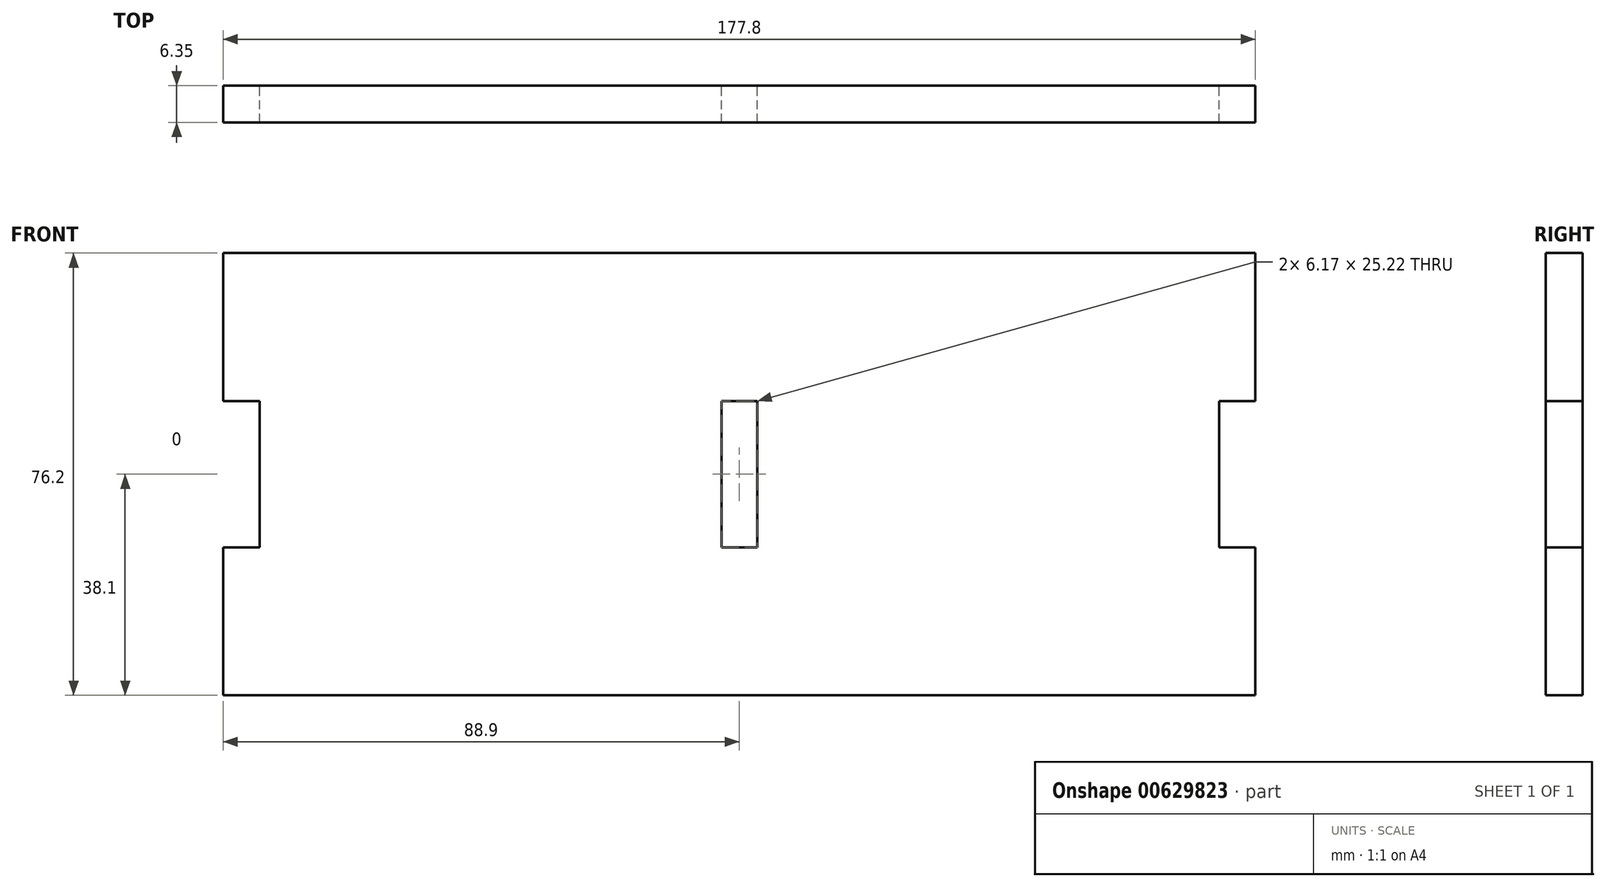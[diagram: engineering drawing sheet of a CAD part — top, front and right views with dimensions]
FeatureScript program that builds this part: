
annotation { "Feature Type Name" : "Feature", "Feature Type Description" : "" }
export const myFeature = defineFeature(function(context is Context, id is Id, definition is map)
    precondition{}
    {
        {
            var Q0;
            Q0=qCreatedBy(makeId("Front.planeOp"),FACE);
            var sketch = newSketch(context, id + "F0", { "sketchPlane" : qUnion([Q0])});
            skLineSegment(sketch, "E0.bottom", {"start": v(0, 0) * mm, "end": v(177.8, 0) * mm});
            skLineSegment(sketch, "E0.top", {"start": v(0, 76.2) * mm, "end": v(177.8, 76.2) * mm});
            skLineSegment(sketch, "E0.left", {"start": v(0, 0) * mm, "end": v(0, 76.2) * mm});
            skLineSegment(sketch, "E0.right", {"start": v(177.8, 0) * mm, "end": v(177.8, 76.2) * mm});
            skLineSegment(sketch, "E1.bottom", {"start": v(25.31, 0) * mm, "end": v(50.89, 0) * mm});
            skLineSegment(sketch, "E1.top", {"start": v(25.31, -6.44) * mm, "end": v(50.89, -6.44) * mm});
            skLineSegment(sketch, "E1.left", {"start": v(25.31, 0) * mm, "end": v(25.31, -6.44) * mm});
            skLineSegment(sketch, "E1.right", {"start": v(50.89, 0) * mm, "end": v(50.89, -6.44) * mm});
            skLineSegment(sketch, "E2.bottom", {"start": v(76.11, 0) * mm, "end": v(101.69, 0) * mm});
            skLineSegment(sketch, "E2.top", {"start": v(76.11, -6.44) * mm, "end": v(101.69, -6.44) * mm});
            skLineSegment(sketch, "E2.left", {"start": v(76.11, 0) * mm, "end": v(76.11, -6.44) * mm});
            skLineSegment(sketch, "E2.right", {"start": v(101.69, 0) * mm, "end": v(101.69, -6.44) * mm});
            skLineSegment(sketch, "E3.bottom", {"start": v(126.91, 0) * mm, "end": v(152.49, 0) * mm});
            skLineSegment(sketch, "E3.top", {"start": v(126.91, -6.44) * mm, "end": v(152.49, -6.44) * mm});
            skLineSegment(sketch, "E3.left", {"start": v(126.91, 0) * mm, "end": v(126.91, -6.44) * mm});
            skLineSegment(sketch, "E3.right", {"start": v(152.49, 0) * mm, "end": v(152.49, -6.44) * mm});
            skPoint(sketch, "E4", {"position": v(38.1, 0) * mm});
            skPoint(sketch, "E5", {"position": v(88.9, 0) * mm});
            skPoint(sketch, "E6", {"position": v(139.7, 0) * mm});
            skLineSegment(sketch, "E7.bottom", {"start": v(177.8, 50.71) * mm, "end": v(171.54, 50.71) * mm});
            skLineSegment(sketch, "E7.top", {"start": v(177.8, 25.49) * mm, "end": v(171.54, 25.49) * mm});
            skLineSegment(sketch, "E7.left", {"start": v(177.8, 50.71) * mm, "end": v(177.8, 25.49) * mm});
            skLineSegment(sketch, "E7.right", {"start": v(171.54, 50.71) * mm, "end": v(171.54, 25.49) * mm});
            skPoint(sketch, "E8", {"position": v(171.54, 38.1) * mm});
            skLineSegment(sketch, "E9.bottom", {"start": v(0, 50.71) * mm, "end": v(6.26, 50.71) * mm});
            skLineSegment(sketch, "E9.top", {"start": v(0, 25.49) * mm, "end": v(6.26, 25.49) * mm});
            skLineSegment(sketch, "E9.right", {"start": v(6.26, 50.71) * mm, "end": v(6.26, 25.49) * mm});
            skPoint(sketch, "E10", {"position": v(6.26, 38.1) * mm});
            skLineSegment(sketch, "E11.bottom", {"start": v(85.81, 50.71) * mm, "end": v(91.99, 50.71) * mm});
            skLineSegment(sketch, "E11.top", {"start": v(85.81, 25.49) * mm, "end": v(91.99, 25.49) * mm});
            skLineSegment(sketch, "E11.left", {"start": v(85.81, 50.71) * mm, "end": v(85.81, 25.49) * mm});
            skLineSegment(sketch, "E11.right", {"start": v(91.99, 50.71) * mm, "end": v(91.99, 25.49) * mm});
            skPoint(sketch, "E12", {"position": v(85.81, 38.1) * mm});
            skPoint(sketch, "E13", {"position": v(88.9, 25.49) * mm});
            skSolve(sketch);
        }
        {
            var Q0;
            {var subQ2=sQuery(id+"F0.wireOp",EDGE,"E0.top");Q0=makeQuery(id+"F0.imprint","IMPRINT",FACE,{"disambiguationData":[TD([[makeQuery(id+"F0.imprint","IMPRINT",EDGE,{"derivedFrom":subQ2}),-1.0]])]});}
            var Q1;
            Q1=makeQuery(id+"F0.imprint","IMPRINT",FACE,{"disambiguationData":[TD([[makeQuery(id+"F0.imprint","IMPRINT",EDGE,{"derivedFrom":sQuery(id+"F0.wireOp",EDGE,"E1.bottom")}),-1.0]])]});
            var Q2;
            Q2=makeQuery(id+"F0.imprint","IMPRINT",FACE,{"disambiguationData":[TD([[makeQuery(id+"F0.imprint","IMPRINT",EDGE,{"derivedFrom":sQuery(id+"F0.wireOp",EDGE,"E2.bottom")}),-1.0]])]});
            var Q3;
            Q3=makeQuery(id+"F0.imprint","IMPRINT",FACE,{"disambiguationData":[TD([[makeQuery(id+"F0.imprint","IMPRINT",EDGE,{"derivedFrom":sQuery(id+"F0.wireOp",EDGE,"E3.bottom")}),-1.0]])]});
            extrude(context, id + "F1", {"entities" : qUnion([Q0, Q1, Q2, Q3]), "depth" : 6.35 * mm, "offsetDistance" : 25.4 * mm});
        }
    });
